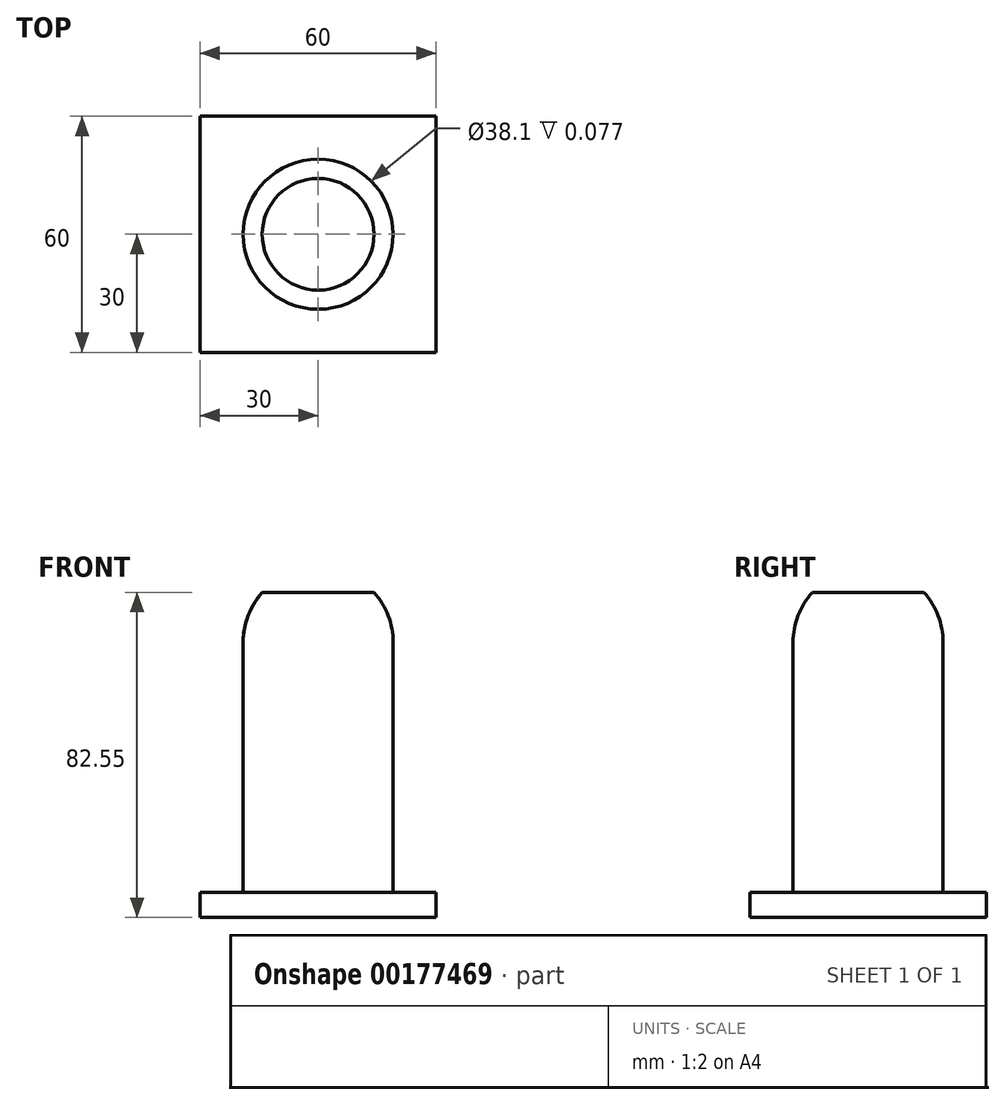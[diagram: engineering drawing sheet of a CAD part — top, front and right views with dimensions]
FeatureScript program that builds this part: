
annotation { "Feature Type Name" : "Feature", "Feature Type Description" : "" }
export const myFeature = defineFeature(function(context is Context, id is Id, definition is map)
    precondition{}
    {
        {
            var Q0;
            Q0=qCreatedBy(makeId("Top.planeOp"),FACE);
            var sketch = newSketch(context, id + "F0", { "sketchPlane" : qUnion([Q0])});
            skLineSegment(sketch, "E0.bottom", {"start": v(30, -30) * mm, "end": v(-30, -30) * mm});
            skLineSegment(sketch, "E0.top", {"start": v(30, 30) * mm, "end": v(-30, 30) * mm});
            skLineSegment(sketch, "E0.left", {"start": v(30, -30) * mm, "end": v(30, 30) * mm});
            skLineSegment(sketch, "E0.right", {"start": v(-30, -30) * mm, "end": v(-30, 30) * mm});
            skPoint(sketch, "E0.middle", {"position": v(0, 0) * mm});
            skCircle(sketch, "E1", {"center": v(0, 0) * mm, "radius": 19.05 * mm});
            skSolve(sketch);
        }
        {
            var Q0;
            Q0=makeQuery(id+"F0.imprint","IMPRINT",FACE,{"disambiguationData":[TD([[makeQuery(id+"F0.imprint","IMPRINT",EDGE,{"derivedFrom":sQuery(id+"F0.wireOp",EDGE,"E0.bottom")}),-1.0]])]});
            extrude(context, id + "F1", {"entities" : qUnion([Q0]), "depth" : 6.35 * mm});
        }
        {
            var Q0;
            Q0=qCreatedBy(makeId("Front.planeOp"),FACE);
            var sketch = newSketch(context, id + "F2", { "sketchPlane" : qUnion([Q0])});
            skLineSegment(sketch, "E2", {"start": v(0, 0) * mm, "end": v(43.58, 0) * mm});
            skLineSegment(sketch, "E3", {"start": v(0, 0) * mm, "end": v(0, 82.55) * mm});
            skLineSegment(sketch, "E4.0", {"start": v(0, 82.55) * mm, "end": v(14.2, 82.55) * mm});
            skLineSegment(sketch, "E5.0", {"start": v(19.05, 0) * mm, "end": v(19.05, 69.84) * mm});
            skLineSegment(sketch, "E6.0", {"start": v(0, 6.35) * mm, "end": v(43.58, 6.35) * mm});
            skLineSegment(sketch, "E7.0", {"start": v(0, 6.27) * mm, "end": v(43.58, 6.27) * mm});
            skLineSegment(sketch, "E8.0", {"start": v(0, 69.84) * mm, "end": v(19.05, 69.84) * mm});
            skArc(sketch, "E9", {"start": v(19.05, 69.84) * mm, "mid": v(17.8, 76.64) * mm, "end": v(14.2, 82.55) * mm});
            skLineSegment(sketch, "E10", {"start": v(0, 82.55) * mm, "end": v(0, 114.12) * mm});
            skSolve(sketch);
        }
        {
            var Q0;
            {var subQ0=sQuery(id+"F2.wireOp",EDGE,"E3");var subQ1=sQuery(id+"F2.wireOp",EDGE,"E2");var subQ2=makeQuery(id+"F2.imprint","INTERSECT",VERTEX,{"derivedFrom":[subQ1,subQ0]});Q0=makeQuery(id+"F2.imprint","IMPRINT",FACE,{"disambiguationData":[TD([[makeQuery(id+"F2.imprint","IMPRINT",EDGE,{"disambiguationData":[TD([[subQ2,-1.0]])],"derivedFrom":subQ1}),1.0]])]});}
            var Q1;
            {var subQ3=sQuery(id+"F2.wireOp",EDGE,"E8.0");Q1=makeQuery(id+"F2.imprint","IMPRINT",FACE,{"disambiguationData":[TD([[makeQuery(id+"F2.imprint","IMPRINT",EDGE,{"derivedFrom":subQ3}),-1.0]])]});}
            var Q2;
            {var subQ0=sQuery(id+"F2.wireOp",EDGE,"E4.0");Q2=makeQuery(id+"F2.imprint","IMPRINT",FACE,{"disambiguationData":[TD([[makeQuery(id+"F2.imprint","IMPRINT",EDGE,{"derivedFrom":subQ0}),-1.0]])]});}
            var Q3;
            Q3=sQuery(id+"F2.wireOp",EDGE,"E10");
            revolve(context, id + "F3", {"operationType" : NewBodyOperationType.ADD, "entities" : qUnion([Q0, Q1, Q2]), "axis" : qUnion([Q3]), "revolveType" : RevolveType.FULL});
        }
    });
